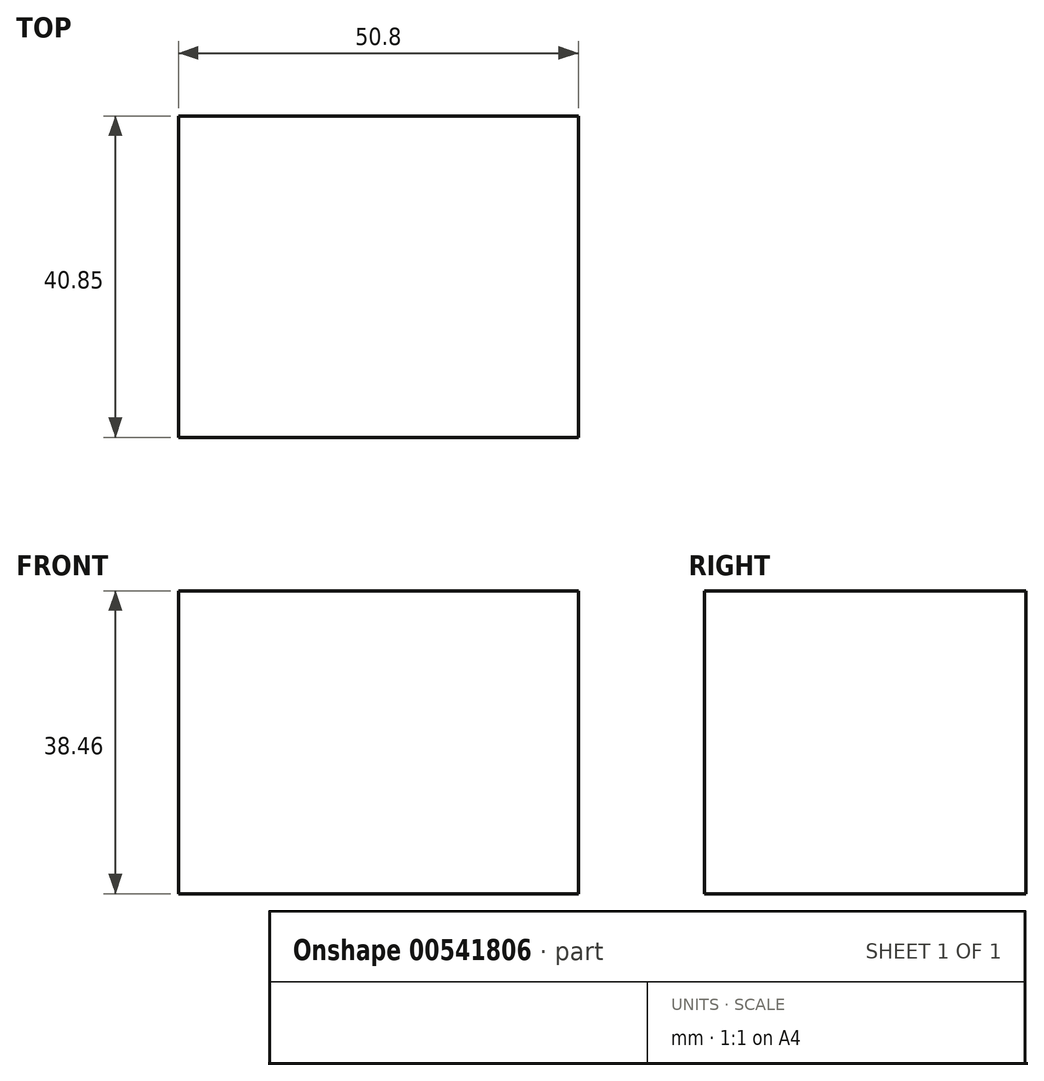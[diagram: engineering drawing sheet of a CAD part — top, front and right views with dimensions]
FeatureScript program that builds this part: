
annotation { "Feature Type Name" : "Feature", "Feature Type Description" : "" }
export const myFeature = defineFeature(function(context is Context, id is Id, definition is map)
    precondition{}
    {
        {
            var Q0;
            Q0=qCreatedBy(makeId("Right.planeOp"),FACE);
            var sketch = newSketch(context, id + "F0", { "sketchPlane" : qUnion([Q0])});
            skLineSegment(sketch, "E0.bottom", {"start": v(0, 0) * mm, "end": v(-40.85, 0) * mm});
            skLineSegment(sketch, "E0.top", {"start": v(0, 38.46) * mm, "end": v(-40.85, 38.46) * mm});
            skLineSegment(sketch, "E0.left", {"start": v(0, 0) * mm, "end": v(0, 38.46) * mm});
            skLineSegment(sketch, "E0.right", {"start": v(-40.85, 0) * mm, "end": v(-40.85, 38.46) * mm});
            skSolve(sketch);
        }
        {
            var Q0;
            Q0 = qSketchRegion(id + "F0", true);
            extrude(context, id + "F1", {"entities" : qUnion([Q0]), "depth" : 50.8 * mm, "offsetDistance" : 25.4 * mm});
        }
    });
